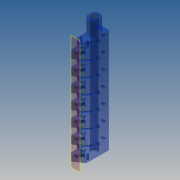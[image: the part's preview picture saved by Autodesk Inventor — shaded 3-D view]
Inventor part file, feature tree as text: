
AUTODESK INVENTOR PART (.ipt)
format: ipt  version: 2012 (Build 160160000, 160)  size: 580,096 bytes
history: native  units: mm
features: sketch x23, hole x12, extrude x9, other x6, plane x5, mirror x2, thread x2, reference x2, pattern_linear x1, fillet x1, revolve x1
ambient origin geometry x8: Origin, YZ Plane, XZ Plane, XY Plane, X Axis, Y Axis, Z Axis, Center Point
bodies: Volumenkörper1 (feature_tree)
feature tree (64):
  extrude  "Extrusion1"  Depth=40.0mm
  hole  "Bohrung1"  [1 undecoded]
  hole  "Bohrung2"  [1 undecoded]
  hole  "Bohrung3"  [1 undecoded]
  hole  "Bohrung4"  [1 undecoded]
  extrude  "Extrusion2"  Depth=8.5mm
  hole  "Bohrung5"  [1 undecoded]
  hole  "Bohrung6"  [1 undecoded]
  plane  "Arbeitsebene1"
  extrude  "Extrusion3"  Depth=5.5mm
  hole  "Bohrung7"  [1 undecoded]
  hole  "Bohrung8"  [1 undecoded]
  plane  "Arbeitsebene2"
  extrude  "Extrusion4"  Depth=8.0mm
  hole  "Bohrung9"  [1 undecoded]
  hole  "Bohrung10"  [1 undecoded]
  pattern_linear  "Rechteckige Anordnung3"  Spacing1=10.0mm  [1 undecoded]
  hole  "Bohrung11"  [1 undecoded]
  plane  "Arbeitsebene3"
  extrude  "Extrusion6"  TaperAngle=90.0deg  [1 undecoded]
  fillet  "Rundung1"  Radius=15.0mm
  hole  "Bohrung13"  [1 undecoded]
  extrude  "Extrusion7"  Depth=1.0mm
  mirror  "Spiegeln1"
  extrude  "Extrusion8"  Depth=10.0mm TaperAngle=0.0deg
  revolve  "Umdrehung2"
  extrude  "Extrusion9"  Depth=10.0mm TaperAngle=0.0deg
  thread  "Gewinde1"  [1 undecoded]
  plane  "Arbeitsebene4"
  mirror  "Spiegeln2"
  sketch  "Skizze25"  dims[d94=-15.0mm]
  plane  "Arbeitsebene5"
  other  "Fläche verschieben1"
  extrude  "Extrusion10"  Depth=4.0mm
  thread  "Gewinde2"  [1 undecoded]
  sketch  "Skizze1"  dims[d0=13.0mm d1=40.0mm]
  sketch  "Skizze2"  dims[d2=120.0mm d3=0.0mm d4=29.5mm]
  sketch  "Skizze3"  dims[d5=5.25mm d6=5.0mm]
  sketch  "Skizze4"  dims[d7=5.0mm]
  sketch  "Skizze5"  dims[d8=2.459mm d9=4.0mm d10=4.0mm d11=2.0mm d12=90.0deg d13=5.0mm d14=20.594885mm d15=5.25mm]
  sketch  "Skizze6"  dims[d16=29.5mm d17=15.0mm]
  sketch  "Skizze7"  dims[d18=15.0mm]
  sketch  "Skizze8"  dims[d19=2.459mm d20=4.0mm d21=4.0mm d22=2.0mm d23=90.0deg d24=5.0mm d25=20.594885mm d26=8.5mm]
  sketch  "Skizze9"  dims[d27=1.2mm d28=4.0mm d29=4.0mm d30=2.0mm d31=90.0deg d32=5.0mm d33=20.594885mm d35=8.5mm]
  sketch  "Skizze10"  dims[d36=15.0mm]
  sketch  "Skizze11"  dims[d37=1.2mm d38=4.0mm d39=4.0mm d40=2.0mm d41=90.0deg d42=5.0mm d43=20.594885mm d44=8.0mm]
  sketch  "Skizze12"  dims[d45=6.5mm d46=5.5mm]
  sketch  "Skizze13"  dims[d48=0.6mm d49=105.0mm d50=0.0mm]
  sketch  "Skizze14"  dims[d57=8.0mm d58=5.0mm]
  sketch  "Skizze15"  dims[d59=1.8mm d60=6.0mm d61=4.0mm d62=2.0mm d63=90.0deg d64=2.0mm d65=20.594885mm d66=8.0mm]
  other  "Arbeitsachse1"
  sketch  "Skizze18"  dims[d67=15.0mm]
  sketch  "Skizze19"  dims[d68=1.8mm d69=6.0mm d70=4.0mm d71=2.0mm d72=90.0deg d73=2.0mm d74=20.594885mm d75=-5.0mm]
  reference  "Referenz1"
  reference  "Referenz2"
  sketch  "Skizze21"  dims[d76=1.8mm d77=6.108652mm]
  sketch  "Skizze22"  dims[d78=10.0mm d79=0.0mm]
  sketch  "Skizze23"  dims[d80=1.8mm d81=6.0mm d82=4.0mm d83=2.0mm d84=90.0deg d85=14.3mm d86=20.594885mm]
  sketch  "Skizze24"  dims[d87=4.134mm d88=3.0mm d89=4.0mm d90=2.0mm d91=90.0deg d92=4.0mm d93=20.594885mm]
  sketch  "Skizze26"  dims[d95=6.108652mm d96=10.0mm d97=0.0mm d98=1.8mm d99=3.0mm d100=4.0mm d101=2.0mm d102=90.0deg d103=14.3mm d104=20.594885mm d105=4.134mm d106=3.0mm d107=4.0mm d108=2.0mm d109=90.0deg d110=4.0mm d111=20.594885mm d112=50.0mm d114=20.0mm d115=8.566mm d116=3.0mm d117=4.0mm d118=2.0mm d119=90.0deg d120=10.0mm d121=20.594885mm d122=90.0deg d137=15.0mm d138=20.0mm d139=0.0mm d140=1.0mm d141=2.459mm d142=6.0mm d143=4.0mm d144=2.0mm d145=90.0deg d146=8.0mm d147=20.594885mm d155=10.0mm d156=0.0mm d157=10.0mm d158=0.0mm d159=67.5deg d160=4.0mm d161=2.1mm d162=90.0deg d163=8.0mm d164=12.0mm d165=0.0mm d169=8.0mm d170=0.0mm d171=-70.0mm d172=-39.1mm d173=8.8mm d174=8.0mm d175=0.0mm d176=10.0mm d177=0.0mm]
  other  "Schnittkanten projizieren1"
  other  "Schnittkanten projizieren2"
  other  "Schnittkanten projizieren3"
  other  "Schnittkanten projizieren5"
note: 16 required parameter values undecoded (feature->parameter linkage not recoverable at this tier; creation-order binding heuristic only, values carry confidence <= 0.55)
